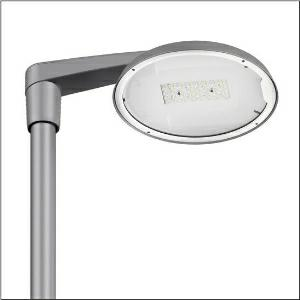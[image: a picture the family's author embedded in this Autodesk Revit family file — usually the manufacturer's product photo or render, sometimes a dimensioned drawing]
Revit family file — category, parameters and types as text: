
# Revit family: dl_r__50_iq_mini___st0_5a_5xa248b41f08he_56c2
name_source: partatom
category: Lighting Fixtures
units: mm (PartAtom-declared; Revit-internal decimal feet)

## family parameters
Cut with Voids When Loaded = No
Host = Face
Light Source = No
Part Type = Normal
Room Calculation Point = No
Round Connector Dimension = Use Diameter
Shared = No

## types (1)
- --- (1 x LED, 9400 lm, 64.6 W, 4000K)
    Apparent Load = 65 VA
    CIE Flux Codes = 41 75 97 100 100
    Color Rendering = 70
    Color Temperature = 4000K
    Default Elevation = 1800 mm
    Description = DL® 50 iQ mini, mast luminaire, primary light control with lens, of PMMA, primary optical cover: cover, of toughened safety glass, transparent, light distribution: ST0.5a, light emission: direct distribution, primary light characteristic: asymmetric, installation type: side-entry, post-top, LED, High Power LED, rated luminous flux: 9.400lm, luminous efficacy: 146lm/W, light colour: 740, colour temperature: 4000K, control gear: iQ Street-Remote, control: optimised constant luminous flux control (CLO 2.0), Desk-Remote (wireless, voltage-free reading and setting of iQ features in the workshop via application-optimized NFC function/RFID function), Light-Fading, Smart-Wire, Night-Set, Lumen-Switch, Temp-Guard, Auto-Match, Street-Remote, mains connection: 230..240V, AC, 50/60Hz, connection cable pre-assembled, cable length: 8,5m, start of lifetime: 65W, end of service life: 68W, reduction: 29W, luminaire housing, of diecast aluminium, powder-coated, Siteco® metallic grey (DB 702S), inclination adjustable: 0°, 5°, 10° (post-top) | 0°, -5°, -10°, -15° (side-entry), please order mast post-top element or mast side-entry element separately, diameter: 500mm, height: 115mm, post-top: for spigot size d x l = 76 x 100mm; with reducer (optional accessory) 60 x 100mm | side-entry: for spigot size d x l = 60 x 100mm; with reducer (optional accessory) 42 x 100mm, mounting height: 4..6m, protection rating (complete): IP66, insulation class (complete): insulation class II (safety insulation), certification: CE, ENEC, ENEC+, VDE, impact resistance: IK08, permissible operating ambient temperature for outdoor applications: -25..+40°C, standard-compliant lighting for roads and squares, packaging unit: 1 piece

Light Distribution: ST0.5a
    Height = 115 mm
    Lamp = 1 x LED
    Lamp Light Flux = 9400 lm
    Lamp Power = 64.6 W
    Lamp count = 1
    Length = 500 mm
    Luminous efficacy = 146 lm/W
    Manufacturer = Siteco
    ModVariant = No
    Model = 5XA248B41F08HE
    Number of Poles = 1
    OnlyDefault = Yes
    Power Factor = 1
    Product Name = DL® 50 iQ mini | ST0.5a
    Product group = mast luminaire | pylon top
    ProductGroupID = 6100
    Protection Class = Protection class II
    Protection Degree = IP 66
    RLX_Detail_Level = 1
    RLX_Emergency_Light_Flux = 0 lm
    RLX_Emergency_Type = 0
    RLX_Emergency_Type_DB = No
    RlxData = <blob elided: 127093 chars, md5=75376739>
    Socket = socket
    Standby Power = 0 W
    System Light Flux = 9400 lm
    System Power = 65 W
    Type Comments = factory setting: luminous flux: 100 % | dim-lin: 254 | 655 mA
    Type Image = l_1251794.jpg
    URL = http://relux.com
    VarID = @adj_143186
    Voltage = 0 V
    Weight = 0.00 kg
    Width = 0 mm  [stored 0 ft]

note: [stored X ft] marks values corroborated as IEEE doubles in the binary element streams (Revit-internal decimal feet)

## geometry (parser evidence)
native form markers: Blend x4, Sweep x10
no freeform markers — native parametric forms only
